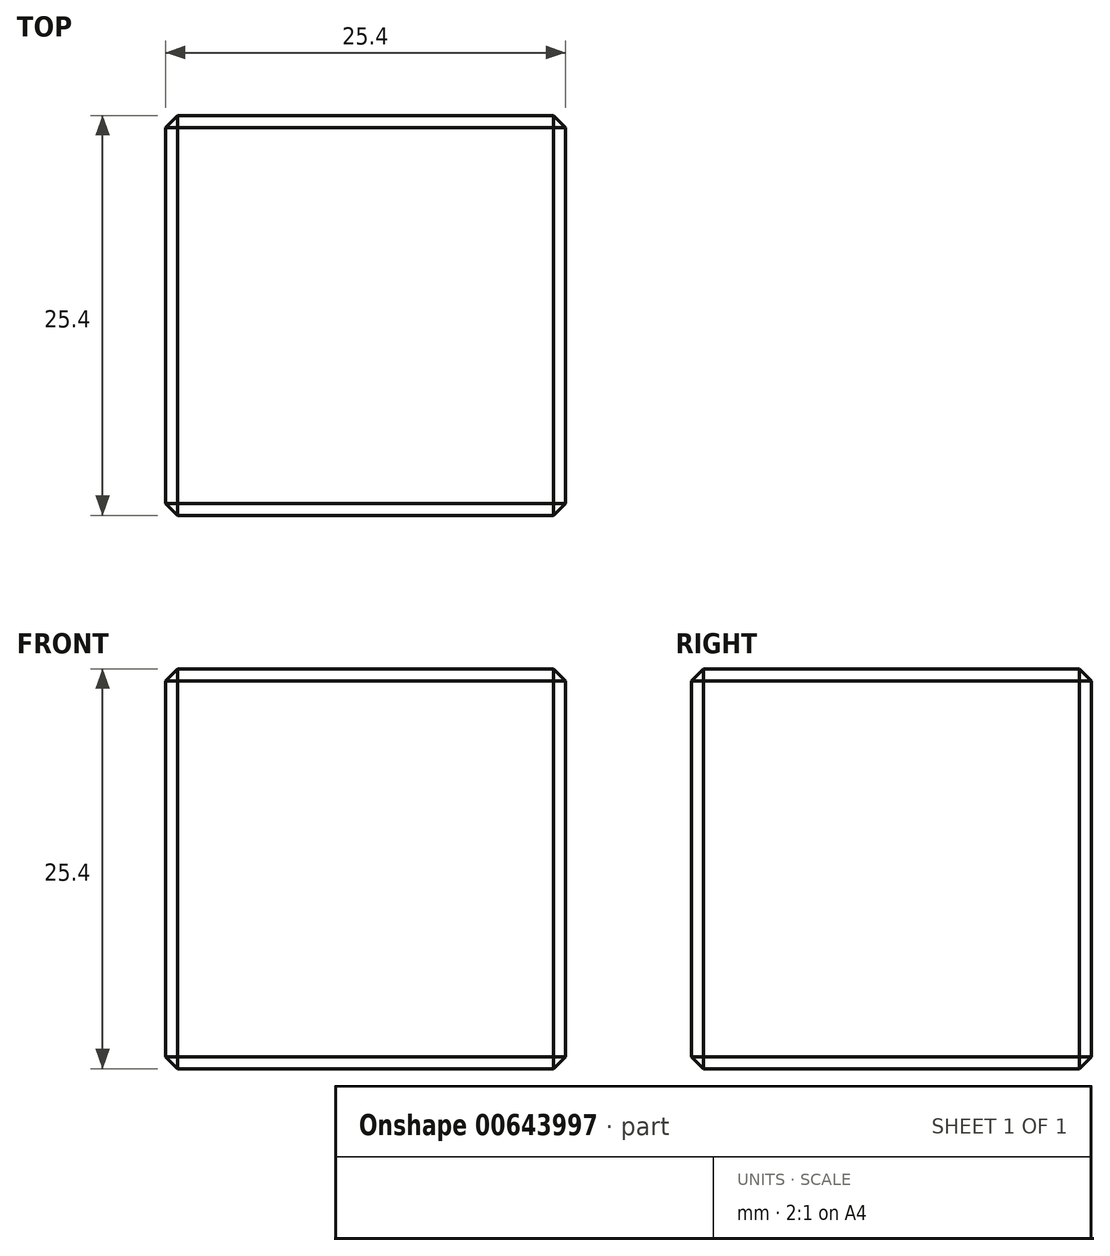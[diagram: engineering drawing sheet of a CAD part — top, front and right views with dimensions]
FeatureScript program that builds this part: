
annotation { "Feature Type Name" : "Feature", "Feature Type Description" : "" }
export const myFeature = defineFeature(function(context is Context, id is Id, definition is map)
    precondition{}
    {
        {
            var Q0;
            Q0=qCreatedBy(makeId("Front.planeOp"),FACE);
            var sketch = newSketch(context, id + "F0", { "sketchPlane" : qUnion([Q0])});
            skLineSegment(sketch, "E0.bottom", {"start": v(12.7, 12.7) * mm, "end": v(-12.7, 12.7) * mm});
            skLineSegment(sketch, "E0.top", {"start": v(12.7, -12.7) * mm, "end": v(-12.7, -12.7) * mm});
            skLineSegment(sketch, "E0.left", {"start": v(12.7, 12.7) * mm, "end": v(12.7, -12.7) * mm});
            skLineSegment(sketch, "E0.right", {"start": v(-12.7, 12.7) * mm, "end": v(-12.7, -12.7) * mm});
            skPoint(sketch, "E0.middle", {"position": v(0, 0) * mm});
            skSolve(sketch);
        }
        {
            var Q0;
            Q0=makeQuery(id+"F0.imprint","IMPRINT",FACE,{"disambiguationData":[TD([[makeQuery(id+"F0.imprint","IMPRINT",EDGE,{"derivedFrom":sQuery(id+"F0.wireOp",EDGE,"E0.bottom")}),1.0]])]});
            extrude(context, id + "F1", {"entities" : qUnion([Q0]), "endBound" : BoundingType.SYMMETRIC, "depth" : 25.4 * mm, "offsetDistance" : 25.4 * mm});
        }
        {
            var Q0;
            Q0=makeQuery(id+"F1.opExtrude","CAP_EDGE",EDGE,{"disambiguationData":[OSD([sQuery(id+"F0.wireOp",EDGE,"E0.bottom")])],"isStart":true});
            var Q1;
            Q1=makeQuery(id+"F1.opExtrude","SWEPT_EDGE",EDGE,{"disambiguationData":[OSD([sQuery(id+"F0.wireOp",EDGE,"E0.bottom"),sQuery(id+"F0.wireOp",EDGE,"E0.right")])]});
            var Q2;
            Q2=makeQuery(id+"F1.opExtrude","CAP_EDGE",EDGE,{"disambiguationData":[OSD([sQuery(id+"F0.wireOp",EDGE,"E0.bottom")])],"isStart":false});
            var Q3;
            Q3=makeQuery(id+"F1.opExtrude","SWEPT_FACE",FACE,{"disambiguationData":[OSD([sQuery(id+"F0.wireOp",EDGE,"E0.bottom")])]});
            var Q4;
            Q4=makeQuery(id+"F1.opExtrude","SWEPT_FACE",FACE,{"disambiguationData":[OSD([sQuery(id+"F0.wireOp",EDGE,"E0.left")])]});
            var Q5;
            Q5=makeQuery(id+"F1.opExtrude","CAP_FACE",FACE,{"disambiguationData":[OSD([sQuery(id+"F0.wireOp",EDGE,"E0.bottom"),sQuery(id+"F0.wireOp",EDGE,"E0.top"),sQuery(id+"F0.wireOp",EDGE,"E0.left"),sQuery(id+"F0.wireOp",EDGE,"E0.right")])],"isStart":false});
            var Q6;
            Q6=makeQuery(id+"F1.opExtrude","SWEPT_FACE",FACE,{"disambiguationData":[OSD([sQuery(id+"F0.wireOp",EDGE,"E0.right")])]});
            var Q7;
            Q7=makeQuery(id+"F1.opExtrude","CAP_FACE",FACE,{"disambiguationData":[OSD([sQuery(id+"F0.wireOp",EDGE,"E0.bottom"),sQuery(id+"F0.wireOp",EDGE,"E0.top"),sQuery(id+"F0.wireOp",EDGE,"E0.left"),sQuery(id+"F0.wireOp",EDGE,"E0.right")])],"isStart":true});
            chamfer(context, id + "F2", {"entities" : qUnion([Q0, Q1, Q2, Q3, Q4, Q5, Q6, Q7]), "width" : 0.76 * mm, "tangentPropagation" : true});
        }
    });
